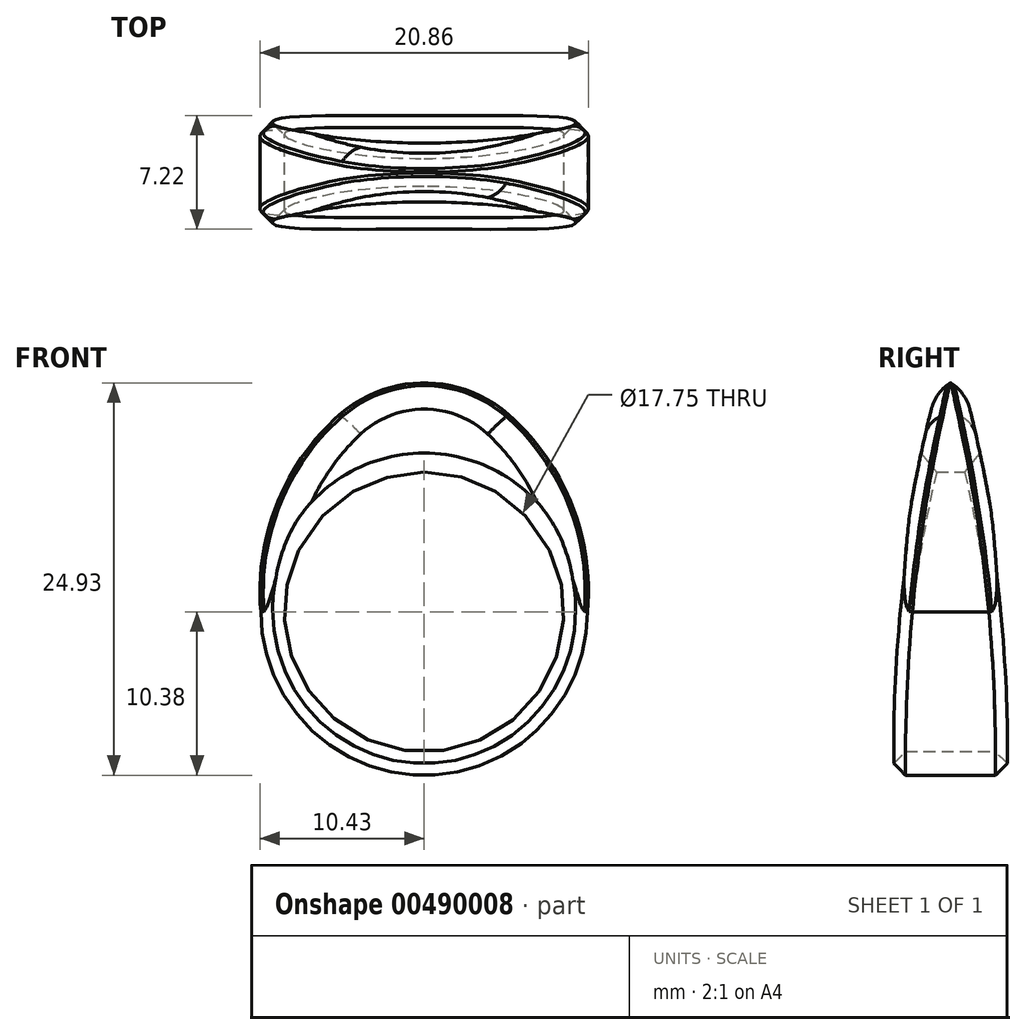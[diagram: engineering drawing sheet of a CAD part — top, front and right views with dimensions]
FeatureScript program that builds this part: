
annotation { "Feature Type Name" : "Feature", "Feature Type Description" : "" }
export const myFeature = defineFeature(function(context is Context, id is Id, definition is map)
    precondition{}
    {
        {
            var Q0;
            Q0=qCreatedBy(makeId("Front.planeOp"),FACE);
            var sketch = newSketch(context, id + "F0", { "sketchPlane" : qUnion([Q0])});
            skCircle(sketch, "E0", {"center": v(0, 0) * mm, "radius": 8.88 * mm});
            skCircle(sketch, "E1.0", {"center": v(0, 0) * mm, "radius": 10.38 * mm});
            skArc(sketch, "E2", {"start": v(0, 15.56) * mm, "mid": v(-7.92, 9.6) * mm, "end": v(-10.37, 0) * mm});
            skArc(sketch, "E3.MirrorCS", {"start": v(0, 15.56) * mm, "mid": v(7.92, 9.6) * mm, "end": v(10.37, 0) * mm});
            skSolve(sketch);
        }
        {
            var Q0;
            Q0=makeQuery(id+"F0.imprint","IMPRINT",FACE,{"disambiguationData":[TD([[makeQuery(id+"F0.imprint","IMPRINT",EDGE,{"derivedFrom":sQuery(id+"F0.wireOp",EDGE,"E0")}),-1.0]])]});
            var Q1;
            {var subQ0=sQuery(id+"F0.wireOp",EDGE,"E2");Q1=makeQuery(id+"F0.imprint","IMPRINT",FACE,{"disambiguationData":[TD([[makeQuery(id+"F0.imprint","IMPRINT",EDGE,{"derivedFrom":subQ0}),1.0]])]});}
            extrude(context, id + "F1", {"entities" : qUnion([Q0, Q1]), "depth" : 4 * mm, "hasSecondDirection" : true, "secondDirectionOppositeDirection" : true, "secondDirectionDepth" : 4 * mm});
        }
        {
            var Q0;
            Q0=qCreatedBy(makeId("Right.planeOp"),FACE);
            var sketch = newSketch(context, id + "F2", { "sketchPlane" : qUnion([Q0])});
            skArc(sketch, "E4", {"start": v(0, 17.32) * mm, "mid": v(-3.06, 3.2) * mm, "end": v(-3.83, -11.2) * mm});
            skArc(sketch, "E5.MirrorCS", {"start": v(0, 17.32) * mm, "mid": v(3.06, 3.2) * mm, "end": v(3.83, -11.2) * mm});
            skLineSegment(sketch, "E6", {"start": v(-3.83, -11.2) * mm, "end": v(-12.28, 0) * mm});
            skLineSegment(sketch, "E7", {"start": v(-12.28, 0) * mm, "end": v(-3.83, 20.7) * mm});
            skLineSegment(sketch, "E8", {"start": v(-3.83, 20.7) * mm, "end": v(3.83, 20.7) * mm});
            skLineSegment(sketch, "E9", {"start": v(3.83, 20.7) * mm, "end": v(11.47, 0) * mm});
            skLineSegment(sketch, "E10", {"start": v(11.47, 0) * mm, "end": v(3.83, -11.2) * mm});
            skSolve(sketch);
        }
        {
            var Q0;
            Q0 = qSketchRegion(id + "F2", true);
            extrude(context, id + "F3", {"entities" : qUnion([Q0]), "operationType" : NewBodyOperationType.REMOVE, "oppositeDirection" : true, "depth" : 25 * mm, "hasSecondDirection" : true, "secondDirectionOppositeDirection" : false, "secondDirectionDepth" : 25 * mm});
        }
        {
            var Q0;
            Q0=makeQuery(id+"F1.opExtrude","SWEPT_EDGE",EDGE,{"disambiguationData":[OSD([sQuery(id+"F0.wireOp",EDGE,"E2"),sQuery(id+"F0.wireOp",EDGE,"E3.MirrorCS")])]});
            fillet(context, id + "F4", {"entities" : qUnion([Q0]), "radius" : 8.1 * mm, "tangentPropagation" : true, "allowEdgeOverflow" : false});
        }
        {
            var Q0;
            Q0=makeQuery(id+"F3.boolean.opBoolean","INTERSECT",EDGE,{"derivedFrom":[makeQuery(id+"F1.opExtrude","SWEPT_FACE",FACE,{"disambiguationData":[OSD([sQuery(id+"F0.wireOp",EDGE,"E0")])]}),makeQuery(id+"F3.opExtrude","SWEPT_FACE",FACE,{"disambiguationData":[OSD([sQuery(id+"F2.wireOp",EDGE,"E5.MirrorCS")])]})]});
            var Q1;
            Q1=makeQuery(id+"F3.boolean.opBoolean","INTERSECT",EDGE,{"derivedFrom":[makeQuery(id+"F1.opExtrude","SWEPT_FACE",FACE,{"disambiguationData":[OSD([sQuery(id+"F0.wireOp",EDGE,"E0")])]}),makeQuery(id+"F3.opExtrude","SWEPT_FACE",FACE,{"disambiguationData":[OSD([sQuery(id+"F2.wireOp",EDGE,"E4")])]})]});
            chamfer(context, id + "F5", {"entities" : qUnion([Q0, Q1]), "width" : 1 * mm, "tangentPropagation" : true});
        }
        {
            var Q0;
            Q0=makeQuery(id+"F3.boolean.opBoolean","INTERSECT",EDGE,{"derivedFrom":[makeQuery(id+"F1.opExtrude","SWEPT_FACE",FACE,{"disambiguationData":[OSD([sQuery(id+"F0.wireOp",EDGE,"E2")])]}),makeQuery(id+"F3.opExtrude","SWEPT_FACE",FACE,{"disambiguationData":[OSD([sQuery(id+"F2.wireOp",EDGE,"E5.MirrorCS")])]})]});
            var Q1;
            Q1=makeQuery(id+"F3.boolean.opBoolean","INTERSECT",EDGE,{"derivedFrom":[makeQuery(id+"F1.opExtrude","SWEPT_FACE",FACE,{"disambiguationData":[OSD([sQuery(id+"F0.wireOp",EDGE,"E2")])]}),makeQuery(id+"F3.opExtrude","SWEPT_FACE",FACE,{"disambiguationData":[OSD([sQuery(id+"F2.wireOp",EDGE,"E4")])]})]});
            var Q2;
            Q2=makeQuery(id+"F3.boolean.opBoolean","INTERSECT",EDGE,{"derivedFrom":[makeQuery(id+"F1.opExtrude","SWEPT_FACE",FACE,{"disambiguationData":[OSD([sQuery(id+"F0.wireOp",EDGE,"E1.0")])]}),makeQuery(id+"F3.opExtrude","SWEPT_FACE",FACE,{"disambiguationData":[OSD([sQuery(id+"F2.wireOp",EDGE,"E4")])]})]});
            var Q3;
            Q3=makeQuery(id+"F3.boolean.opBoolean","INTERSECT",EDGE,{"derivedFrom":[makeQuery(id+"F1.opExtrude","SWEPT_FACE",FACE,{"disambiguationData":[OSD([sQuery(id+"F0.wireOp",EDGE,"E1.0")])]}),makeQuery(id+"F3.opExtrude","SWEPT_FACE",FACE,{"disambiguationData":[OSD([sQuery(id+"F2.wireOp",EDGE,"E5.MirrorCS")])]})]});
            chamfer(context, id + "F6", {"entities" : qUnion([Q0, Q1, Q2, Q3]), "width" : 1 * mm, "tangentPropagation" : true});
        }
        {
            var Q0;
            {var subQ0=makeQuery(id+"F3.boolean.opBoolean","COPY",FACE,{"derivedFrom":makeQuery(id+"F3.opExtrude","SWEPT_FACE",FACE,{"disambiguationData":[OSD([sQuery(id+"F2.wireOp",EDGE,"E5.MirrorCS")])]})});Q0=makeQuery(id+"F6.opChamfer","BLEND_EDGE",EDGE,{"blendedFrom":[makeQuery(id+"F4.opFillet","BLEND_EDGE",EDGE,{"blendedFrom":[makeQuery(id+"F1.opExtrude","SWEPT_EDGE",EDGE,{"disambiguationData":[OSD([sQuery(id+"F0.wireOp",EDGE,"E2"),sQuery(id+"F0.wireOp",EDGE,"E3.MirrorCS")])]}),subQ0],"blendedInto":[subQ0]}),subQ0],"blendedInto":[subQ0]});}
            var Q1;
            {var subQ0=makeQuery(id+"F3.boolean.opBoolean","COPY",FACE,{"derivedFrom":makeQuery(id+"F3.opExtrude","SWEPT_FACE",FACE,{"disambiguationData":[OSD([sQuery(id+"F2.wireOp",EDGE,"E4")])]})});Q1=makeQuery(id+"F6.opChamfer","BLEND_EDGE",EDGE,{"blendedFrom":[makeQuery(id+"F4.opFillet","BLEND_EDGE",EDGE,{"blendedFrom":[makeQuery(id+"F1.opExtrude","SWEPT_EDGE",EDGE,{"disambiguationData":[OSD([sQuery(id+"F0.wireOp",EDGE,"E2"),sQuery(id+"F0.wireOp",EDGE,"E3.MirrorCS")])]}),subQ0],"blendedInto":[subQ0]}),subQ0],"blendedInto":[subQ0]});}
            fillet(context, id + "F7", {"entities" : qUnion([Q0, Q1]), "radius" : 2.7 * mm, "tangentPropagation" : true, "allowEdgeOverflow" : false});
        }
    });
